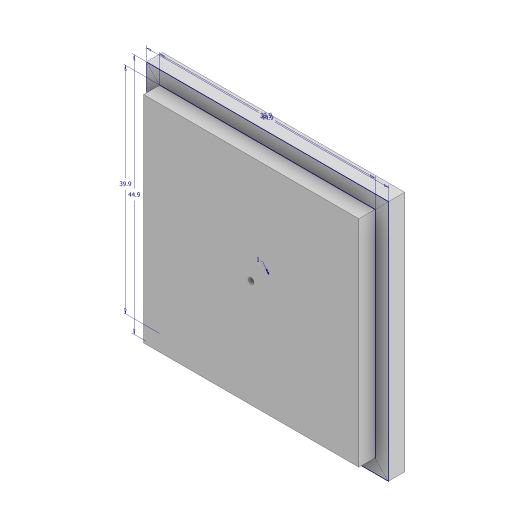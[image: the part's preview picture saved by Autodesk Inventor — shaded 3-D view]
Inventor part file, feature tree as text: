
AUTODESK INVENTOR PART (.ipt)
format: ipt  version: 2023 (Build 270158000, 158)  size: 112,640 bytes
history: native  units: in
note: dims shown in document units (in); Inventor stores cm internally (conversion verified against a paired STEP export)
features: extrude x2, sketch x1
ambient origin geometry x8: Origin, YZ Plane, XZ Plane, XY Plane, X Axis, Y Axis, Z Axis, Center Point
bodies: Solid1 (feature_tree)
feature tree (3):
  sketch  "Sketch1"  dims[d2=1.5709in d3=1.5709in d4=0.0394in d5=1.7677in d6=1.7677in d7=0.1181in d8=0.0in d9=0.1181in d10=0.0in]
  extrude  "Extrusion1"  Depth=1.5709in
  extrude  "Extrusion2"  Depth=0.1181in
